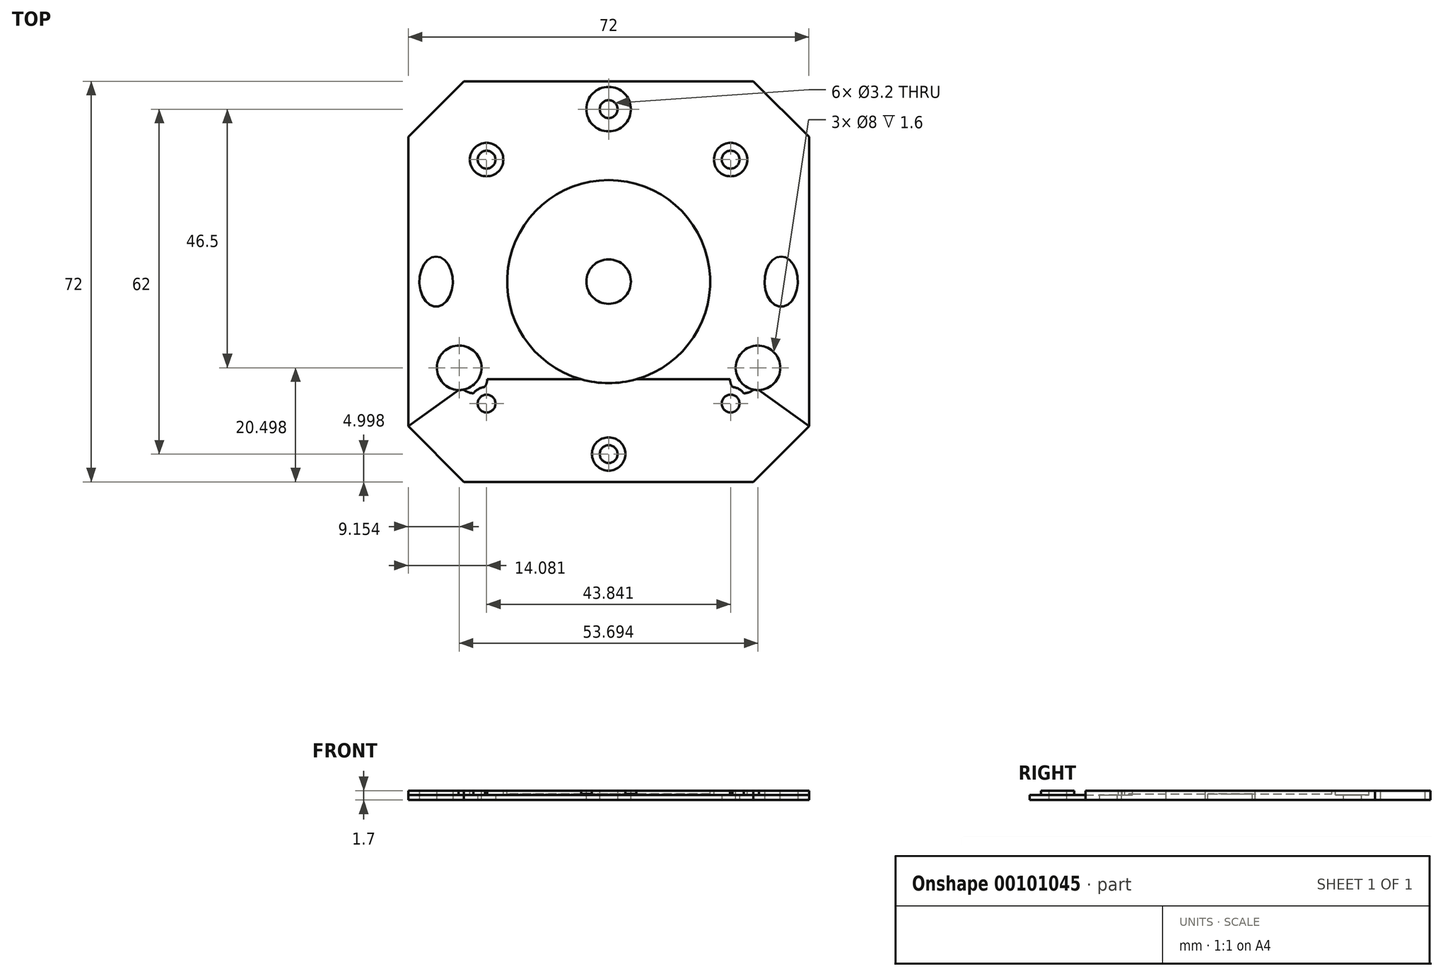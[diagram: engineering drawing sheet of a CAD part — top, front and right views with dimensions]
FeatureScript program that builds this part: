
annotation { "Feature Type Name" : "Feature", "Feature Type Description" : "" }
export const myFeature = defineFeature(function(context is Context, id is Id, definition is map)
    precondition{}
    {
        {
            var Q0;
            Q0=qCreatedBy(makeId("Top.planeOp"),FACE);
            var sketch = newSketch(context, id + "F0", { "sketchPlane" : qUnion([Q0])});
            skLineSegment(sketch, "E0.bottom", {"start": v(-39.14, 42.5) * mm, "end": v(12.86, 42.5) * mm});
            skLineSegment(sketch, "E0.top", {"start": v(-39.14, -29.5) * mm, "end": v(12.86, -29.5) * mm});
            skLineSegment(sketch, "E0.left", {"start": v(-49.14, 32.5) * mm, "end": v(-49.14, -19.5) * mm});
            skLineSegment(sketch, "E0.right", {"start": v(22.86, 32.5) * mm, "end": v(22.86, -19.5) * mm});
            skLineSegment(sketch, "E1", {"start": v(-49.14, 42.5) * mm, "end": v(22.86, -29.5) * mm, "construction": true});
            skLineSegment(sketch, "E2", {"start": v(22.86, 42.5) * mm, "end": v(-49.14, -29.5) * mm, "construction": true});
            skLineSegment(sketch, "E3.bottom", {"start": v(-35.06, 28.43) * mm, "end": v(8.78, 28.43) * mm});
            skLineSegment(sketch, "E3.top", {"start": v(-35.06, -15.41) * mm, "end": v(8.78, -15.41) * mm});
            skLineSegment(sketch, "E3.left", {"start": v(-35.06, 28.43) * mm, "end": v(-35.06, -15.41) * mm});
            skLineSegment(sketch, "E3.right", {"start": v(8.78, 28.43) * mm, "end": v(8.78, -15.41) * mm});
            skCircle(sketch, "E4", {"center": v(-35.06, 28.43) * mm, "radius": 1.6 * mm});
            skCircle(sketch, "E5", {"center": v(8.78, 28.43) * mm, "radius": 1.6 * mm});
            skCircle(sketch, "E6", {"center": v(8.78, -15.41) * mm, "radius": 1.6 * mm});
            skCircle(sketch, "E7", {"center": v(-35.06, -15.41) * mm, "radius": 1.6 * mm});
            skLineSegment(sketch, "E8", {"start": v(-13.14, 42.5) * mm, "end": v(-13.14, -29.5) * mm, "construction": true});
            skLineSegment(sketch, "E9", {"start": v(-49.14, 6.5) * mm, "end": v(22.86, 6.5) * mm, "construction": true});
            skLineSegment(sketch, "E10", {"start": v(-44.14, 6.5) * mm, "end": v(-13.14, 37.5) * mm});
            skLineSegment(sketch, "E11", {"start": v(-13.14, 37.5) * mm, "end": v(17.86, 6.5) * mm});
            skLineSegment(sketch, "E12", {"start": v(-13.14, -24.5) * mm, "end": v(17.86, 6.5) * mm});
            skLineSegment(sketch, "E13", {"start": v(-13.14, -24.5) * mm, "end": v(-44.14, 6.5) * mm});
            skCircle(sketch, "E14", {"center": v(-13.14, 37.5) * mm, "radius": 1.6 * mm});
            skCircle(sketch, "E15", {"center": v(17.86, 6.5) * mm, "radius": 1.6 * mm});
            skCircle(sketch, "E16", {"center": v(-13.14, -24.5) * mm, "radius": 1.6 * mm});
            skCircle(sketch, "E17", {"center": v(-44.14, 6.5) * mm, "radius": 1.6 * mm});
            skCircle(sketch, "E18", {"center": v(-13.14, 6.5) * mm, "radius": 18.25 * mm});
            skPoint(sketch, "E19.visualSharp", {"position": v(-49.14, 42.5) * mm});
            skPoint(sketch, "E20.visualSharp", {"position": v(22.86, 42.5) * mm});
            skPoint(sketch, "E21.visualSharp", {"position": v(22.86, -29.5) * mm});
            skPoint(sketch, "E22.visualSharp", {"position": v(-49.14, -29.5) * mm});
            skLineSegment(sketch, "E23", {"start": v(-39.14, 42.5) * mm, "end": v(-49.14, 32.5) * mm});
            skLineSegment(sketch, "E24", {"start": v(12.86, 42.5) * mm, "end": v(22.86, 32.5) * mm});
            skLineSegment(sketch, "E25", {"start": v(22.86, -19.5) * mm, "end": v(12.86, -29.5) * mm});
            skLineSegment(sketch, "E26", {"start": v(-39.14, -29.5) * mm, "end": v(-49.14, -19.5) * mm});
            skSolve(sketch);
        }
        {
            var Q0;
            Q0=makeQuery(id+"F0.imprint","IMPRINT",FACE,{"disambiguationData":[TD([[makeQuery(id+"F0.imprint","IMPRINT",EDGE,{"derivedFrom":sQuery(id+"F0.wireOp",EDGE,"E0.bottom")}),-1.0]])]});
            var Q1;
            {var subQ0=sQuery(id+"F0.wireOp",EDGE,"E4");var subQ1=sQuery(id+"F0.wireOp",EDGE,"E3.bottom");var subQ2=makeQuery(id+"F0.imprint","INTERSECT",VERTEX,{"derivedFrom":[subQ1,subQ0]});Q1=makeQuery(id+"F0.imprint","IMPRINT",FACE,{"disambiguationData":[TD([[makeQuery(id+"F0.imprint","IMPRINT",EDGE,{"disambiguationData":[TD([[subQ2,-1.0]])],"derivedFrom":subQ1}),-1.0]])]});}
            var Q2;
            {var subQ0=sQuery(id+"F0.wireOp",EDGE,"E10");var subQ1=sQuery(id+"F0.wireOp",EDGE,"E3.bottom");var subQ2=makeQuery(id+"F0.imprint","INTERSECT",VERTEX,{"derivedFrom":[subQ1,subQ0]});Q2=makeQuery(id+"F0.imprint","IMPRINT",FACE,{"disambiguationData":[TD([[makeQuery(id+"F0.imprint","IMPRINT",EDGE,{"disambiguationData":[TD([[subQ2,-1.0]])],"derivedFrom":subQ1}),1.0]])]});}
            var Q3;
            {var subQ0=sQuery(id+"F0.wireOp",EDGE,"E11");var subQ1=sQuery(id+"F0.wireOp",EDGE,"E3.bottom");var subQ2=makeQuery(id+"F0.imprint","INTERSECT",VERTEX,{"derivedFrom":[subQ1,subQ0]});Q3=makeQuery(id+"F0.imprint","IMPRINT",FACE,{"disambiguationData":[TD([[makeQuery(id+"F0.imprint","IMPRINT",EDGE,{"disambiguationData":[TD([[subQ2,-1.0]])],"derivedFrom":subQ1}),-1.0]])]});}
            var Q4;
            {var subQ0=sQuery(id+"F0.wireOp",EDGE,"E11");var subQ1=sQuery(id+"F0.wireOp",EDGE,"E3.right");var subQ2=makeQuery(id+"F0.imprint","INTERSECT",VERTEX,{"derivedFrom":[subQ1,subQ0]});Q4=makeQuery(id+"F0.imprint","IMPRINT",FACE,{"disambiguationData":[TD([[makeQuery(id+"F0.imprint","IMPRINT",EDGE,{"disambiguationData":[TD([[subQ2,-1.0]])],"derivedFrom":subQ1}),1.0]])]});}
            var Q5;
            {var subQ0=sQuery(id+"F0.wireOp",EDGE,"E12");var subQ1=sQuery(id+"F0.wireOp",EDGE,"E3.top");var subQ2=makeQuery(id+"F0.imprint","INTERSECT",VERTEX,{"derivedFrom":[subQ1,subQ0]});Q5=makeQuery(id+"F0.imprint","IMPRINT",FACE,{"disambiguationData":[TD([[makeQuery(id+"F0.imprint","IMPRINT",EDGE,{"disambiguationData":[TD([[subQ2,-1.0]])],"derivedFrom":subQ1}),1.0]])]});}
            var Q6;
            {var subQ0=sQuery(id+"F0.wireOp",EDGE,"E13");var subQ1=sQuery(id+"F0.wireOp",EDGE,"E3.top");var subQ2=makeQuery(id+"F0.imprint","INTERSECT",VERTEX,{"derivedFrom":[subQ1,subQ0]});Q6=makeQuery(id+"F0.imprint","IMPRINT",FACE,{"disambiguationData":[TD([[makeQuery(id+"F0.imprint","IMPRINT",EDGE,{"disambiguationData":[TD([[subQ2,-1.0]])],"derivedFrom":subQ1}),-1.0]])]});}
            var Q7;
            {var subQ0=sQuery(id+"F0.wireOp",EDGE,"E7");var subQ1=sQuery(id+"F0.wireOp",EDGE,"E3.top");var subQ2=makeQuery(id+"F0.imprint","INTERSECT",VERTEX,{"derivedFrom":[subQ1,subQ0]});Q7=makeQuery(id+"F0.imprint","IMPRINT",FACE,{"disambiguationData":[TD([[makeQuery(id+"F0.imprint","IMPRINT",EDGE,{"disambiguationData":[TD([[subQ2,-1.0]])],"derivedFrom":subQ1}),1.0]])]});}
            var Q8;
            {var subQ0=sQuery(id+"F0.wireOp",EDGE,"E10");var subQ1=sQuery(id+"F0.wireOp",EDGE,"E3.left");var subQ2=makeQuery(id+"F0.imprint","INTERSECT",VERTEX,{"derivedFrom":[subQ1,subQ0]});Q8=makeQuery(id+"F0.imprint","IMPRINT",FACE,{"disambiguationData":[TD([[makeQuery(id+"F0.imprint","IMPRINT",EDGE,{"disambiguationData":[TD([[subQ2,-1.0]])],"derivedFrom":subQ1}),-1.0]])]});}
            var Q9;
            Q9=makeQuery(id+"F0.imprint","IMPRINT",FACE,{"disambiguationData":[TD([[makeQuery(id+"F0.imprint","IMPRINT",EDGE,{"derivedFrom":sQuery(id+"F0.wireOp",EDGE,"E18")}),-1.0]])]});
            var Q10;
            Q10=makeQuery(id+"F0.imprint","IMPRINT",FACE,{"disambiguationData":[TD([[makeQuery(id+"F0.imprint","IMPRINT",EDGE,{"derivedFrom":sQuery(id+"F0.wireOp",EDGE,"E18")}),1.0]])]});
            extrude(context, id + "F1", {"entities" : qUnion([Q0, Q1, Q2, Q3, Q4, Q5, Q6, Q7, Q8, Q9, Q10]), "depth" : 1.7 * mm});
        }
        {
            var Q0;
            Q0=makeQuery(id+"F1.opExtrude","CAP_FACE",FACE,{"disambiguationData":[OSD([sQuery(id+"F0.wireOp",EDGE,"E0.bottom"),sQuery(id+"F0.wireOp",EDGE,"E0.top"),sQuery(id+"F0.wireOp",EDGE,"E0.left"),sQuery(id+"F0.wireOp",EDGE,"E0.right"),sQuery(id+"F0.wireOp",EDGE,"E4"),sQuery(id+"F0.wireOp",EDGE,"E5"),sQuery(id+"F0.wireOp",EDGE,"E6"),sQuery(id+"F0.wireOp",EDGE,"E7"),sQuery(id+"F0.wireOp",EDGE,"E14"),sQuery(id+"F0.wireOp",EDGE,"E15"),sQuery(id+"F0.wireOp",EDGE,"E16"),sQuery(id+"F0.wireOp",EDGE,"E17"),sQuery(id+"F0.wireOp",EDGE,"E23"),sQuery(id+"F0.wireOp",EDGE,"E24"),sQuery(id+"F0.wireOp",EDGE,"E25"),sQuery(id+"F0.wireOp",EDGE,"E26")])],"isStart":false});
            var sketch = newSketch(context, id + "F2", { "sketchPlane" : qUnion([Q0])});
            skLineSegment(sketch, "E27", {"start": v(-49.14, 6.5) * mm, "end": v(22.86, 6.5) * mm});
            skLineSegment(sketch, "E28", {"start": v(-13.14, -29.5) * mm, "end": v(-13.14, 42.5) * mm});
            skCircle(sketch, "E29", {"center": v(-13.14, 6.5) * mm, "radius": 18.25 * mm});
            skSolve(sketch);
        }
        {
            var Q0;
            {var subQ0=sQuery(id+"F2.wireOp",EDGE,"E29");var subQ1=sQuery(id+"F2.wireOp",EDGE,"E27");var subQ2=makeQuery(id+"F2.imprint","INTERSECT",VERTEX,{"disambiguationData":[OD(0.0)],"derivedFrom":[subQ1,subQ0]});Q0=makeQuery(id+"F2.imprint","IMPRINT",FACE,{"disambiguationData":[TD([[makeQuery(id+"F2.imprint","IMPRINT",EDGE,{"disambiguationData":[TD([[subQ2,-1.0]])],"derivedFrom":subQ1}),1.0]])]});}
            var Q1;
            {var subQ0=sQuery(id+"F2.wireOp",EDGE,"E28");var subQ1=sQuery(id+"F2.wireOp",EDGE,"E27");var subQ2=makeQuery(id+"F2.imprint","INTERSECT",VERTEX,{"derivedFrom":[subQ1,subQ0]});Q1=makeQuery(id+"F2.imprint","IMPRINT",FACE,{"disambiguationData":[TD([[makeQuery(id+"F2.imprint","IMPRINT",EDGE,{"disambiguationData":[TD([[subQ2,-1.0]])],"derivedFrom":subQ1}),-1.0]])]});}
            var Q2;
            {var subQ0=sQuery(id+"F2.wireOp",EDGE,"E28");var subQ1=sQuery(id+"F2.wireOp",EDGE,"E27");var subQ2=makeQuery(id+"F2.imprint","INTERSECT",VERTEX,{"derivedFrom":[subQ1,subQ0]});Q2=makeQuery(id+"F2.imprint","IMPRINT",FACE,{"disambiguationData":[TD([[makeQuery(id+"F2.imprint","IMPRINT",EDGE,{"disambiguationData":[TD([[subQ2,-1.0]])],"derivedFrom":subQ1}),1.0]])]});}
            var Q3;
            {var subQ0=sQuery(id+"F2.wireOp",EDGE,"E29");var subQ1=sQuery(id+"F2.wireOp",EDGE,"E27");var subQ2=makeQuery(id+"F2.imprint","INTERSECT",VERTEX,{"disambiguationData":[OD(0.0)],"derivedFrom":[subQ1,subQ0]});Q3=makeQuery(id+"F2.imprint","IMPRINT",FACE,{"disambiguationData":[TD([[makeQuery(id+"F2.imprint","IMPRINT",EDGE,{"disambiguationData":[TD([[subQ2,-1.0]])],"derivedFrom":subQ1}),-1.0]])]});}
            extrude(context, id + "F3", {"entities" : qUnion([Q0, Q1, Q2, Q3]), "operationType" : NewBodyOperationType.REMOVE, "oppositeDirection" : true, "depth" : 0.6 * mm});
        }
        {
            var Q0;
            Q0=makeQuery(id+"F1.opExtrude","CAP_FACE",FACE,{"disambiguationData":[OSD([sQuery(id+"F0.wireOp",EDGE,"E0.bottom"),sQuery(id+"F0.wireOp",EDGE,"E0.top"),sQuery(id+"F0.wireOp",EDGE,"E0.left"),sQuery(id+"F0.wireOp",EDGE,"E0.right"),sQuery(id+"F0.wireOp",EDGE,"E4"),sQuery(id+"F0.wireOp",EDGE,"E5"),sQuery(id+"F0.wireOp",EDGE,"E6"),sQuery(id+"F0.wireOp",EDGE,"E7"),sQuery(id+"F0.wireOp",EDGE,"E14"),sQuery(id+"F0.wireOp",EDGE,"E15"),sQuery(id+"F0.wireOp",EDGE,"E16"),sQuery(id+"F0.wireOp",EDGE,"E17"),sQuery(id+"F0.wireOp",EDGE,"E23"),sQuery(id+"F0.wireOp",EDGE,"E24"),sQuery(id+"F0.wireOp",EDGE,"E25"),sQuery(id+"F0.wireOp",EDGE,"E26")])],"isStart":false});
            var sketch = newSketch(context, id + "F4", { "sketchPlane" : qUnion([Q0])});
            skLineSegment(sketch, "E30", {"start": v(-49.14, 6.5) * mm, "end": v(22.86, 6.5) * mm});
            skLineSegment(sketch, "E31", {"start": v(-13.14, -29.5) * mm, "end": v(-13.14, 42.5) * mm});
            skCircle(sketch, "E32", {"center": v(-13.14, 6.5) * mm, "radius": 3.5 * mm});
            skLineSegment(sketch, "E33", {"start": v(-49.14, -19.5) * mm, "end": v(22.86, 32.5) * mm});
            skLineSegment(sketch, "E34", {"start": v(22.86, -19.5) * mm, "end": v(-49.14, 32.5) * mm});
            skLineSegment(sketch, "E35", {"start": v(-13.14, 6.5) * mm, "end": v(-37.46, -11.06) * mm});
            skLineSegment(sketch, "E36", {"start": v(-13.14, 6.5) * mm, "end": v(11.18, 24.07) * mm});
            skLineSegment(sketch, "E37.bottom", {"start": v(-37.46, -11.06) * mm, "end": v(11.18, -11.06) * mm});
            skLineSegment(sketch, "E37.top", {"start": v(-37.46, 24.07) * mm, "end": v(11.18, 24.07) * mm});
            skLineSegment(sketch, "E37.left", {"start": v(-37.46, -11.06) * mm, "end": v(-37.46, 24.07) * mm});
            skLineSegment(sketch, "E37.right", {"start": v(11.18, -11.06) * mm, "end": v(11.18, 24.07) * mm});
            skCircle(sketch, "E38", {"center": v(-37.46, -11.06) * mm, "radius": 2.5 * mm});
            skCircle(sketch, "E39", {"center": v(11.18, -11.06) * mm, "radius": 2.5 * mm});
            skCircle(sketch, "E40", {"center": v(-13.14, 37.5) * mm, "radius": 3 * mm});
            skCircle(sketch, "E41", {"center": v(17.86, 6.5) * mm, "radius": 3 * mm});
            skCircle(sketch, "E42", {"center": v(-44.14, 6.5) * mm, "radius": 3 * mm});
            skCircle(sketch, "E43", {"center": v(-13.14, -24.5) * mm, "radius": 3 * mm});
            skCircle(sketch, "E44", {"center": v(8.78, -15.41) * mm, "radius": 3 * mm});
            skCircle(sketch, "E45", {"center": v(-35.06, 28.43) * mm, "radius": 3 * mm});
            skCircle(sketch, "E46", {"center": v(-35.06, -15.41) * mm, "radius": 3 * mm});
            skCircle(sketch, "E47", {"center": v(8.78, 28.43) * mm, "radius": 3 * mm});
            skSolve(sketch);
        }
        {
            var Q0;
            Q0=makeQuery(id+"F4.imprint","IMPRINT",FACE,{"disambiguationData":[TD([[makeQuery(id+"F4.imprint","IMPRINT",EDGE,{"derivedFrom":makeQuery(id+"F1.opExtrude","CAP_EDGE",EDGE,{"disambiguationData":[OSD([sQuery(id+"F0.wireOp",EDGE,"E4")])],"isStart":false})}),1.0]])]});
            var Q1;
            Q1=makeQuery(id+"F4.imprint","IMPRINT",FACE,{"disambiguationData":[TD([[makeQuery(id+"F4.imprint","IMPRINT",EDGE,{"derivedFrom":makeQuery(id+"F1.opExtrude","CAP_EDGE",EDGE,{"disambiguationData":[OSD([sQuery(id+"F0.wireOp",EDGE,"E5")])],"isStart":false})}),1.0]])]});
            var Q2;
            Q2=makeQuery(id+"F4.imprint","IMPRINT",FACE,{"disambiguationData":[TD([[makeQuery(id+"F4.imprint","IMPRINT",EDGE,{"derivedFrom":makeQuery(id+"F1.opExtrude","CAP_EDGE",EDGE,{"disambiguationData":[OSD([sQuery(id+"F0.wireOp",EDGE,"E6")])],"isStart":false})}),1.0]])]});
            var Q3;
            Q3=makeQuery(id+"F4.imprint","IMPRINT",FACE,{"disambiguationData":[TD([[makeQuery(id+"F4.imprint","IMPRINT",EDGE,{"derivedFrom":makeQuery(id+"F1.opExtrude","CAP_EDGE",EDGE,{"disambiguationData":[OSD([sQuery(id+"F0.wireOp",EDGE,"E7")])],"isStart":false})}),1.0]])]});
            var Q4;
            {var subQ0=sQuery(id+"F4.wireOp",EDGE,"E46");var subQ1=sQuery(id+"F4.wireOp",EDGE,"E38");var subQ2=makeQuery(id+"F4.imprint","INTERSECT",VERTEX,{"disambiguationData":[OD(0.0)],"derivedFrom":[subQ1,subQ0]});Q4=makeQuery(id+"F4.imprint","IMPRINT",FACE,{"disambiguationData":[TD([[makeQuery(id+"F4.imprint","IMPRINT",EDGE,{"disambiguationData":[TD([[subQ2,-1.0]])],"derivedFrom":subQ1}),1.0]])]});}
            var Q5;
            {var subQ0=sQuery(id+"F4.wireOp",EDGE,"E44");var subQ1=sQuery(id+"F4.wireOp",EDGE,"E39");var subQ2=makeQuery(id+"F4.imprint","INTERSECT",VERTEX,{"disambiguationData":[OD(0.0)],"derivedFrom":[subQ1,subQ0]});Q5=makeQuery(id+"F4.imprint","IMPRINT",FACE,{"disambiguationData":[TD([[makeQuery(id+"F4.imprint","IMPRINT",EDGE,{"disambiguationData":[TD([[subQ2,-1.0]])],"derivedFrom":subQ1}),1.0]])]});}
            var Q6;
            Q6=makeQuery(id+"F4.imprint","IMPRINT",FACE,{"disambiguationData":[TD([[makeQuery(id+"F4.imprint","IMPRINT",EDGE,{"derivedFrom":sQuery(id+"F4.wireOp",EDGE,"E45")}),1.0]])]});
            var Q7;
            Q7=makeQuery(id+"F4.imprint","IMPRINT",FACE,{"disambiguationData":[TD([[makeQuery(id+"F4.imprint","IMPRINT",EDGE,{"derivedFrom":sQuery(id+"F4.wireOp",EDGE,"E47")}),1.0]])]});
            var Q8;
            {var subQ1=sQuery(id+"F4.wireOp",EDGE,"E33");var subQ3=sQuery(id+"F4.wireOp",EDGE,"E38");var subQ4=makeQuery(id+"F4.imprint","INTERSECT",VERTEX,{"derivedFrom":[subQ1,subQ3]});Q8=makeQuery(id+"F4.imprint","IMPRINT",FACE,{"disambiguationData":[TD([[makeQuery(id+"F4.imprint","IMPRINT",EDGE,{"disambiguationData":[TD([[subQ4,1.0]])],"derivedFrom":subQ3}),1.0]])]});}
            var Q9;
            {var subQ1=sQuery(id+"F4.wireOp",EDGE,"E34");var subQ3=sQuery(id+"F4.wireOp",EDGE,"E39");var subQ4=makeQuery(id+"F4.imprint","INTERSECT",VERTEX,{"disambiguationData":[OD(0.0)],"derivedFrom":[subQ1,subQ3]});Q9=makeQuery(id+"F4.imprint","IMPRINT",FACE,{"disambiguationData":[TD([[makeQuery(id+"F4.imprint","IMPRINT",EDGE,{"disambiguationData":[TD([[subQ4,-1.0]])],"derivedFrom":subQ3}),1.0]])]});}
            var Q10;
            {var subQ1=sQuery(id+"F4.wireOp",EDGE,"E34");var subQ3=sQuery(id+"F4.wireOp",EDGE,"E39");var subQ4=makeQuery(id+"F4.imprint","INTERSECT",VERTEX,{"disambiguationData":[OD(1.0)],"derivedFrom":[subQ1,subQ3]});Q10=makeQuery(id+"F4.imprint","IMPRINT",FACE,{"disambiguationData":[TD([[makeQuery(id+"F4.imprint","IMPRINT",EDGE,{"disambiguationData":[TD([[subQ4,-1.0]])],"derivedFrom":subQ3}),1.0]])]});}
            var Q11;
            {var subQ1=sQuery(id+"F4.wireOp",EDGE,"E34");var subQ3=sQuery(id+"F4.wireOp",EDGE,"E39");var subQ4=makeQuery(id+"F4.imprint","INTERSECT",VERTEX,{"disambiguationData":[OD(1.0)],"derivedFrom":[subQ1,subQ3]});Q11=makeQuery(id+"F4.imprint","IMPRINT",FACE,{"disambiguationData":[TD([[makeQuery(id+"F4.imprint","IMPRINT",EDGE,{"disambiguationData":[TD([[subQ4,1.0]])],"derivedFrom":subQ3}),1.0]])]});}
            var Q12;
            {var subQ1=sQuery(id+"F4.wireOp",EDGE,"E35");var subQ3=sQuery(id+"F4.wireOp",EDGE,"E38");var subQ4=makeQuery(id+"F4.imprint","INTERSECT",VERTEX,{"derivedFrom":[subQ1,subQ3]});Q12=makeQuery(id+"F4.imprint","IMPRINT",FACE,{"disambiguationData":[TD([[makeQuery(id+"F4.imprint","IMPRINT",EDGE,{"disambiguationData":[TD([[subQ4,1.0]])],"derivedFrom":subQ3}),1.0]])]});}
            var Q13;
            {var subQ1=sQuery(id+"F4.wireOp",EDGE,"E35");var subQ3=sQuery(id+"F4.wireOp",EDGE,"E38");var subQ4=makeQuery(id+"F4.imprint","INTERSECT",VERTEX,{"derivedFrom":[subQ1,subQ3]});Q13=makeQuery(id+"F4.imprint","IMPRINT",FACE,{"disambiguationData":[TD([[makeQuery(id+"F4.imprint","IMPRINT",EDGE,{"disambiguationData":[TD([[subQ4,-1.0]])],"derivedFrom":subQ3}),1.0]])]});}
            var Q14;
            Q14=makeQuery(id+"F4.imprint","IMPRINT",FACE,{"disambiguationData":[TD([[makeQuery(id+"F4.imprint","IMPRINT",EDGE,{"derivedFrom":makeQuery(id+"F1.opExtrude","CAP_EDGE",EDGE,{"disambiguationData":[OSD([sQuery(id+"F0.wireOp",EDGE,"E7")])],"isStart":false})}),-1.0]])]});
            var Q15;
            Q15=makeQuery(id+"F4.imprint","IMPRINT",FACE,{"disambiguationData":[TD([[makeQuery(id+"F4.imprint","IMPRINT",EDGE,{"derivedFrom":makeQuery(id+"F1.opExtrude","CAP_EDGE",EDGE,{"disambiguationData":[OSD([sQuery(id+"F0.wireOp",EDGE,"E6")])],"isStart":false})}),-1.0]])]});
            var Q16;
            {var subQ0=sQuery(id+"F4.wireOp",EDGE,"E38");var subQ6=sQuery(id+"F4.wireOp",EDGE,"E33");var subQ7=makeQuery(id+"F4.imprint","INTERSECT",VERTEX,{"derivedFrom":[subQ6,subQ0]});Q16=makeQuery(id+"F4.imprint","IMPRINT",FACE,{"disambiguationData":[TD([[makeQuery(id+"F4.imprint","IMPRINT",EDGE,{"disambiguationData":[TD([[subQ7,-1.0]])],"derivedFrom":subQ0}),1.0]])]});}
            var Q17;
            {var subQ0=sQuery(id+"F4.wireOp",EDGE,"E39");var subQ5=sQuery(id+"F4.wireOp",EDGE,"E37.bottom");var subQ6=makeQuery(id+"F4.imprint","INTERSECT",VERTEX,{"derivedFrom":[subQ5,subQ0]});Q17=makeQuery(id+"F4.imprint","IMPRINT",FACE,{"disambiguationData":[TD([[makeQuery(id+"F4.imprint","IMPRINT",EDGE,{"disambiguationData":[TD([[subQ6,-1.0]])],"derivedFrom":subQ0}),1.0]])]});}
            var Q18;
            {var subQ0=sQuery(id+"F4.wireOp",EDGE,"E42");var subQ1=sQuery(id+"F4.wireOp",EDGE,"E30");var subQ2=makeQuery(id+"F4.imprint","INTERSECT",VERTEX,{"disambiguationData":[OD(0.0)],"derivedFrom":[subQ1,subQ0]});Q18=makeQuery(id+"F4.imprint","IMPRINT",FACE,{"disambiguationData":[TD([[makeQuery(id+"F4.imprint","IMPRINT",EDGE,{"disambiguationData":[TD([[subQ2,-1.0]])],"derivedFrom":subQ1}),1.0]])]});}
            var Q19;
            {var subQ0=sQuery(id+"F4.wireOp",EDGE,"E42");var subQ1=sQuery(id+"F4.wireOp",EDGE,"E30");var subQ2=makeQuery(id+"F4.imprint","INTERSECT",VERTEX,{"disambiguationData":[OD(0.0)],"derivedFrom":[subQ1,subQ0]});Q19=makeQuery(id+"F4.imprint","IMPRINT",FACE,{"disambiguationData":[TD([[makeQuery(id+"F4.imprint","IMPRINT",EDGE,{"disambiguationData":[TD([[subQ2,-1.0]])],"derivedFrom":subQ1}),-1.0]])]});}
            var Q20;
            {var subQ0=sQuery(id+"F4.wireOp",EDGE,"E41");var subQ1=sQuery(id+"F4.wireOp",EDGE,"E30");var subQ2=makeQuery(id+"F4.imprint","INTERSECT",VERTEX,{"disambiguationData":[OD(0.0)],"derivedFrom":[subQ1,subQ0]});Q20=makeQuery(id+"F4.imprint","IMPRINT",FACE,{"disambiguationData":[TD([[makeQuery(id+"F4.imprint","IMPRINT",EDGE,{"disambiguationData":[TD([[subQ2,-1.0]])],"derivedFrom":subQ1}),1.0]])]});}
            var Q21;
            {var subQ0=sQuery(id+"F4.wireOp",EDGE,"E41");var subQ1=sQuery(id+"F4.wireOp",EDGE,"E30");var subQ2=makeQuery(id+"F4.imprint","INTERSECT",VERTEX,{"disambiguationData":[OD(0.0)],"derivedFrom":[subQ1,subQ0]});Q21=makeQuery(id+"F4.imprint","IMPRINT",FACE,{"disambiguationData":[TD([[makeQuery(id+"F4.imprint","IMPRINT",EDGE,{"disambiguationData":[TD([[subQ2,-1.0]])],"derivedFrom":subQ1}),-1.0]])]});}
            var Q22;
            {var subQ0=sQuery(id+"F4.wireOp",EDGE,"E43");var subQ1=sQuery(id+"F4.wireOp",EDGE,"E31");var subQ2=makeQuery(id+"F4.imprint","INTERSECT",VERTEX,{"disambiguationData":[OD(0.0)],"derivedFrom":[subQ1,subQ0]});Q22=makeQuery(id+"F4.imprint","IMPRINT",FACE,{"disambiguationData":[TD([[makeQuery(id+"F4.imprint","IMPRINT",EDGE,{"disambiguationData":[TD([[subQ2,-1.0]])],"derivedFrom":subQ1}),1.0]])]});}
            var Q23;
            {var subQ0=sQuery(id+"F4.wireOp",EDGE,"E43");var subQ1=sQuery(id+"F4.wireOp",EDGE,"E31");var subQ2=makeQuery(id+"F4.imprint","INTERSECT",VERTEX,{"disambiguationData":[OD(0.0)],"derivedFrom":[subQ1,subQ0]});Q23=makeQuery(id+"F4.imprint","IMPRINT",FACE,{"disambiguationData":[TD([[makeQuery(id+"F4.imprint","IMPRINT",EDGE,{"disambiguationData":[TD([[subQ2,-1.0]])],"derivedFrom":subQ1}),-1.0]])]});}
            var Q24;
            {var subQ0=sQuery(id+"F4.wireOp",EDGE,"E40");var subQ1=sQuery(id+"F4.wireOp",EDGE,"E31");var subQ2=makeQuery(id+"F4.imprint","INTERSECT",VERTEX,{"disambiguationData":[OD(0.0)],"derivedFrom":[subQ1,subQ0]});Q24=makeQuery(id+"F4.imprint","IMPRINT",FACE,{"disambiguationData":[TD([[makeQuery(id+"F4.imprint","IMPRINT",EDGE,{"disambiguationData":[TD([[subQ2,-1.0]])],"derivedFrom":subQ1}),1.0]])]});}
            var Q25;
            {var subQ0=sQuery(id+"F4.wireOp",EDGE,"E40");var subQ1=sQuery(id+"F4.wireOp",EDGE,"E31");var subQ2=makeQuery(id+"F4.imprint","INTERSECT",VERTEX,{"disambiguationData":[OD(0.0)],"derivedFrom":[subQ1,subQ0]});Q25=makeQuery(id+"F4.imprint","IMPRINT",FACE,{"disambiguationData":[TD([[makeQuery(id+"F4.imprint","IMPRINT",EDGE,{"disambiguationData":[TD([[subQ2,-1.0]])],"derivedFrom":subQ1}),-1.0]])]});}
            var Q26;
            {var subQ0=sQuery(id+"F4.wireOp",EDGE,"E30");var subQ1=makeQuery(id+"F1.opExtrude","CAP_EDGE",EDGE,{"disambiguationData":[OSD([sQuery(id+"F0.wireOp",EDGE,"E17")])],"isStart":false});var subQ2=makeQuery(id+"F4.imprint","INTERSECT",VERTEX,{"disambiguationData":[OD(0.0)],"derivedFrom":[subQ1,subQ0]});Q26=makeQuery(id+"F4.imprint","IMPRINT",FACE,{"disambiguationData":[TD([[makeQuery(id+"F4.imprint","IMPRINT",EDGE,{"disambiguationData":[TD([[subQ2,-1.0]])],"derivedFrom":subQ0}),1.0]])]});}
            var Q27;
            {var subQ0=sQuery(id+"F4.wireOp",EDGE,"E30");var subQ1=makeQuery(id+"F1.opExtrude","CAP_EDGE",EDGE,{"disambiguationData":[OSD([sQuery(id+"F0.wireOp",EDGE,"E17")])],"isStart":false});var subQ2=makeQuery(id+"F4.imprint","INTERSECT",VERTEX,{"disambiguationData":[OD(0.0)],"derivedFrom":[subQ1,subQ0]});Q27=makeQuery(id+"F4.imprint","IMPRINT",FACE,{"disambiguationData":[TD([[makeQuery(id+"F4.imprint","IMPRINT",EDGE,{"disambiguationData":[TD([[subQ2,-1.0]])],"derivedFrom":subQ0}),-1.0]])]});}
            var Q28;
            {var subQ0=sQuery(id+"F4.wireOp",EDGE,"E30");var subQ1=makeQuery(id+"F1.opExtrude","CAP_EDGE",EDGE,{"disambiguationData":[OSD([sQuery(id+"F0.wireOp",EDGE,"E15")])],"isStart":false});var subQ2=makeQuery(id+"F4.imprint","INTERSECT",VERTEX,{"disambiguationData":[OD(0.0)],"derivedFrom":[subQ1,subQ0]});Q28=makeQuery(id+"F4.imprint","IMPRINT",FACE,{"disambiguationData":[TD([[makeQuery(id+"F4.imprint","IMPRINT",EDGE,{"disambiguationData":[TD([[subQ2,-1.0]])],"derivedFrom":subQ0}),1.0]])]});}
            var Q29;
            {var subQ0=sQuery(id+"F4.wireOp",EDGE,"E30");var subQ1=makeQuery(id+"F1.opExtrude","CAP_EDGE",EDGE,{"disambiguationData":[OSD([sQuery(id+"F0.wireOp",EDGE,"E15")])],"isStart":false});var subQ2=makeQuery(id+"F4.imprint","INTERSECT",VERTEX,{"disambiguationData":[OD(0.0)],"derivedFrom":[subQ1,subQ0]});Q29=makeQuery(id+"F4.imprint","IMPRINT",FACE,{"disambiguationData":[TD([[makeQuery(id+"F4.imprint","IMPRINT",EDGE,{"disambiguationData":[TD([[subQ2,-1.0]])],"derivedFrom":subQ0}),-1.0]])]});}
            var Q30;
            {var subQ0=sQuery(id+"F4.wireOp",EDGE,"E31");var subQ1=makeQuery(id+"F1.opExtrude","CAP_EDGE",EDGE,{"disambiguationData":[OSD([sQuery(id+"F0.wireOp",EDGE,"E16")])],"isStart":false});var subQ2=makeQuery(id+"F4.imprint","INTERSECT",VERTEX,{"disambiguationData":[OD(0.0)],"derivedFrom":[subQ1,subQ0]});Q30=makeQuery(id+"F4.imprint","IMPRINT",FACE,{"disambiguationData":[TD([[makeQuery(id+"F4.imprint","IMPRINT",EDGE,{"disambiguationData":[TD([[subQ2,-1.0]])],"derivedFrom":subQ0}),1.0]])]});}
            var Q31;
            {var subQ0=sQuery(id+"F4.wireOp",EDGE,"E31");var subQ1=makeQuery(id+"F1.opExtrude","CAP_EDGE",EDGE,{"disambiguationData":[OSD([sQuery(id+"F0.wireOp",EDGE,"E16")])],"isStart":false});var subQ2=makeQuery(id+"F4.imprint","INTERSECT",VERTEX,{"disambiguationData":[OD(0.0)],"derivedFrom":[subQ1,subQ0]});Q31=makeQuery(id+"F4.imprint","IMPRINT",FACE,{"disambiguationData":[TD([[makeQuery(id+"F4.imprint","IMPRINT",EDGE,{"disambiguationData":[TD([[subQ2,-1.0]])],"derivedFrom":subQ0}),-1.0]])]});}
            var Q32;
            {var subQ0=sQuery(id+"F4.wireOp",EDGE,"E31");var subQ1=makeQuery(id+"F1.opExtrude","CAP_EDGE",EDGE,{"disambiguationData":[OSD([sQuery(id+"F0.wireOp",EDGE,"E14")])],"isStart":false});var subQ2=makeQuery(id+"F4.imprint","INTERSECT",VERTEX,{"disambiguationData":[OD(0.0)],"derivedFrom":[subQ1,subQ0]});Q32=makeQuery(id+"F4.imprint","IMPRINT",FACE,{"disambiguationData":[TD([[makeQuery(id+"F4.imprint","IMPRINT",EDGE,{"disambiguationData":[TD([[subQ2,-1.0]])],"derivedFrom":subQ0}),1.0]])]});}
            var Q33;
            {var subQ0=sQuery(id+"F4.wireOp",EDGE,"E31");var subQ1=makeQuery(id+"F1.opExtrude","CAP_EDGE",EDGE,{"disambiguationData":[OSD([sQuery(id+"F0.wireOp",EDGE,"E14")])],"isStart":false});var subQ2=makeQuery(id+"F4.imprint","INTERSECT",VERTEX,{"disambiguationData":[OD(0.0)],"derivedFrom":[subQ1,subQ0]});Q33=makeQuery(id+"F4.imprint","IMPRINT",FACE,{"disambiguationData":[TD([[makeQuery(id+"F4.imprint","IMPRINT",EDGE,{"disambiguationData":[TD([[subQ2,-1.0]])],"derivedFrom":subQ0}),-1.0]])]});}
            extrude(context, id + "F5", {"entities" : qUnion([Q0, Q1, Q2, Q3, Q4, Q5, Q6, Q7, Q8, Q9, Q10, Q11, Q12, Q13, Q14, Q15, Q16, Q17, Q18, Q19, Q20, Q21, Q22, Q23, Q24, Q25, Q26, Q27, Q28, Q29, Q30, Q31, Q32, Q33]), "operationType" : NewBodyOperationType.REMOVE, "oppositeDirection" : true, "depth" : 0.8 * mm});
        }
        {
            var Q0;
            Q0=makeQuery(id+"F1.opExtrude","CAP_FACE",FACE,{"disambiguationData":[OSD([sQuery(id+"F0.wireOp",EDGE,"E0.bottom"),sQuery(id+"F0.wireOp",EDGE,"E0.top"),sQuery(id+"F0.wireOp",EDGE,"E0.left"),sQuery(id+"F0.wireOp",EDGE,"E0.right"),sQuery(id+"F0.wireOp",EDGE,"E4"),sQuery(id+"F0.wireOp",EDGE,"E5"),sQuery(id+"F0.wireOp",EDGE,"E6"),sQuery(id+"F0.wireOp",EDGE,"E7"),sQuery(id+"F0.wireOp",EDGE,"E14"),sQuery(id+"F0.wireOp",EDGE,"E15"),sQuery(id+"F0.wireOp",EDGE,"E16"),sQuery(id+"F0.wireOp",EDGE,"E17"),sQuery(id+"F0.wireOp",EDGE,"E23"),sQuery(id+"F0.wireOp",EDGE,"E24"),sQuery(id+"F0.wireOp",EDGE,"E25"),sQuery(id+"F0.wireOp",EDGE,"E26")])],"isStart":false});
            var sketch = newSketch(context, id + "F6", { "sketchPlane" : qUnion([Q0])});
            skLineSegment(sketch, "E48", {"start": v(-13.14, 42.5) * mm, "end": v(-13.14, -29.5) * mm});
            skLineSegment(sketch, "E49", {"start": v(-49.14, 6.5) * mm, "end": v(22.86, 6.5) * mm});
            skCircle(sketch, "E50", {"center": v(-13.14, 6.5) * mm, "radius": 4 * mm});
            skSolve(sketch);
        }
        {
            var Q0;
            Q0 = qSketchRegion(id + "F6", true);
            extrude(context, id + "F7", {"entities" : qUnion([Q0]), "operationType" : NewBodyOperationType.REMOVE, "oppositeDirection" : true, "depth" : 25 * mm});
        }
        {
            var Q0;
            Q0=makeQuery(id+"F1.opExtrude","CAP_FACE",FACE,{"disambiguationData":[OSD([sQuery(id+"F0.wireOp",EDGE,"E0.bottom"),sQuery(id+"F0.wireOp",EDGE,"E0.top"),sQuery(id+"F0.wireOp",EDGE,"E0.left"),sQuery(id+"F0.wireOp",EDGE,"E0.right"),sQuery(id+"F0.wireOp",EDGE,"E4"),sQuery(id+"F0.wireOp",EDGE,"E5"),sQuery(id+"F0.wireOp",EDGE,"E6"),sQuery(id+"F0.wireOp",EDGE,"E7"),sQuery(id+"F0.wireOp",EDGE,"E14"),sQuery(id+"F0.wireOp",EDGE,"E15"),sQuery(id+"F0.wireOp",EDGE,"E16"),sQuery(id+"F0.wireOp",EDGE,"E17"),sQuery(id+"F0.wireOp",EDGE,"E23"),sQuery(id+"F0.wireOp",EDGE,"E24"),sQuery(id+"F0.wireOp",EDGE,"E25"),sQuery(id+"F0.wireOp",EDGE,"E26")])],"isStart":false});
            var sketch = newSketch(context, id + "F8", { "sketchPlane" : qUnion([Q0])});
            skCircle(sketch, "E51", {"center": v(-37.46, -11.06) * mm, "radius": 2.5 * mm});
            skCircle(sketch, "E52", {"center": v(11.18, -11.06) * mm, "radius": 2.5 * mm});
            skSolve(sketch);
        }
        {
            var Q0;
            Q0 = qSketchRegion(id + "F8", true);
            extrude(context, id + "F9", {"entities" : qUnion([Q0]), "operationType" : NewBodyOperationType.ADD, "oppositeDirection" : true, "depth" : 1.6 * mm});
        }
        {
            var Q0;
            Q0=makeQuery(id+"F9.boolean.opBoolean","MERGE",FACE,{"derivedFrom":[makeQuery(id+"F1.opExtrude","CAP_FACE",FACE,{"disambiguationData":[OSD([sQuery(id+"F0.wireOp",EDGE,"E0.bottom"),sQuery(id+"F0.wireOp",EDGE,"E0.top"),sQuery(id+"F0.wireOp",EDGE,"E0.left"),sQuery(id+"F0.wireOp",EDGE,"E0.right"),sQuery(id+"F0.wireOp",EDGE,"E4"),sQuery(id+"F0.wireOp",EDGE,"E5"),sQuery(id+"F0.wireOp",EDGE,"E6"),sQuery(id+"F0.wireOp",EDGE,"E7"),sQuery(id+"F0.wireOp",EDGE,"E14"),sQuery(id+"F0.wireOp",EDGE,"E15"),sQuery(id+"F0.wireOp",EDGE,"E16"),sQuery(id+"F0.wireOp",EDGE,"E17"),sQuery(id+"F0.wireOp",EDGE,"E23"),sQuery(id+"F0.wireOp",EDGE,"E24"),sQuery(id+"F0.wireOp",EDGE,"E25"),sQuery(id+"F0.wireOp",EDGE,"E26")])],"isStart":false}),makeQuery(id+"F9.opExtrude","CAP_FACE",FACE,{"disambiguationData":[OSD([sQuery(id+"F8.wireOp",EDGE,"E51")])],"isStart":true}),makeQuery(id+"F9.opExtrude","CAP_FACE",FACE,{"disambiguationData":[OSD([sQuery(id+"F8.wireOp",EDGE,"E52")])],"isStart":true})]});
            var sketch = newSketch(context, id + "F10", { "sketchPlane" : qUnion([Q0])});
            skCircle(sketch, "E53", {"center": v(-13.14, 6.5) * mm, "radius": 31 * mm, "construction": true});
            skPoint(sketch, "E53.first.point", {"position": v(-13.14, 37.5) * mm});
            skPoint(sketch, "E53.second.point", {"position": v(17.86, 6.5) * mm});
            skPoint(sketch, "E53.third.point", {"position": v(-35.06, -15.41) * mm});
            skLineSegment(sketch, "E54.0", {"start": v(-13.14, 37.5) * mm, "end": v(13.7, -9) * mm, "construction": true});
            skLineSegment(sketch, "E54.1", {"start": v(13.7, -9) * mm, "end": v(-39.99, -9) * mm, "construction": true});
            skLineSegment(sketch, "E54.2", {"start": v(-39.99, -9) * mm, "end": v(-13.14, 37.5) * mm, "construction": true});
            skCircle(sketch, "E55", {"center": v(-13.14, 37.5) * mm, "radius": 4 * mm});
            skCircle(sketch, "E56", {"center": v(13.7, -9) * mm, "radius": 4 * mm});
            skCircle(sketch, "E57", {"center": v(-39.99, -9) * mm, "radius": 4 * mm});
            skSolve(sketch);
        }
        {
            var Q0;
            Q0=makeQuery(id+"F10.imprint","IMPRINT",FACE,{"disambiguationData":[TD([[makeQuery(id+"F10.imprint","IMPRINT",EDGE,{"derivedFrom":sQuery(id+"F10.wireOp",EDGE,"E56")}),1.0]])]});
            var Q1;
            Q1=makeQuery(id+"F10.imprint","IMPRINT",FACE,{"disambiguationData":[TD([[makeQuery(id+"F10.imprint","IMPRINT",EDGE,{"derivedFrom":sQuery(id+"F10.wireOp",EDGE,"E57")}),1.0]])]});
            var Q2;
            Q2=makeQuery(id+"F10.imprint","IMPRINT",FACE,{"disambiguationData":[TD([[makeQuery(id+"F10.imprint","IMPRINT",EDGE,{"derivedFrom":makeQuery(id+"F5.boolean.opBoolean","COPY",EDGE,{"derivedFrom":makeQuery(id+"F5.opExtrude","CAP_EDGE",EDGE,{"disambiguationData":[OSD([sQuery(id+"F4.wireOp",EDGE,"E40")])],"isStart":true})})}),1.0]])]});
            var Q3;
            Q3=makeQuery(id+"F10.imprint","IMPRINT",FACE,{"disambiguationData":[TD([[makeQuery(id+"F10.imprint","IMPRINT",EDGE,{"derivedFrom":sQuery(id+"F10.wireOp",EDGE,"E55")}),1.0]])]});
            extrude(context, id + "F11", {"entities" : qUnion([Q0, Q1, Q2, Q3]), "operationType" : NewBodyOperationType.REMOVE, "oppositeDirection" : true, "depth" : 1.6 * mm});
        }
        {
            var Q0;
            Q0=makeQuery(id+"F9.boolean.opBoolean","MERGE",FACE,{"derivedFrom":[makeQuery(id+"F1.opExtrude","CAP_FACE",FACE,{"disambiguationData":[OSD([sQuery(id+"F0.wireOp",EDGE,"E0.bottom"),sQuery(id+"F0.wireOp",EDGE,"E0.top"),sQuery(id+"F0.wireOp",EDGE,"E0.left"),sQuery(id+"F0.wireOp",EDGE,"E0.right"),sQuery(id+"F0.wireOp",EDGE,"E4"),sQuery(id+"F0.wireOp",EDGE,"E5"),sQuery(id+"F0.wireOp",EDGE,"E6"),sQuery(id+"F0.wireOp",EDGE,"E7"),sQuery(id+"F0.wireOp",EDGE,"E14"),sQuery(id+"F0.wireOp",EDGE,"E15"),sQuery(id+"F0.wireOp",EDGE,"E16"),sQuery(id+"F0.wireOp",EDGE,"E17"),sQuery(id+"F0.wireOp",EDGE,"E23"),sQuery(id+"F0.wireOp",EDGE,"E24"),sQuery(id+"F0.wireOp",EDGE,"E25"),sQuery(id+"F0.wireOp",EDGE,"E26")])],"isStart":false}),makeQuery(id+"F9.opExtrude","CAP_FACE",FACE,{"disambiguationData":[OSD([sQuery(id+"F8.wireOp",EDGE,"E51")])],"isStart":true}),makeQuery(id+"F9.opExtrude","CAP_FACE",FACE,{"disambiguationData":[OSD([sQuery(id+"F8.wireOp",EDGE,"E52")])],"isStart":true})]});
            var sketch = newSketch(context, id + "F12", { "sketchPlane" : qUnion([Q0])});
            skCircle(sketch, "E58", {"center": v(-35.06, -15.41) * mm, "radius": 3 * mm});
            skCircle(sketch, "E59", {"center": v(8.78, -15.41) * mm, "radius": 3 * mm});
            skSolve(sketch);
        }
        {
            var Q0;
            {var subQ1=makeQuery(id+"F9.opExtrude","CAP_EDGE",EDGE,{"disambiguationData":[OSD([sQuery(id+"F8.wireOp",EDGE,"E52")])],"isStart":true});Q0=makeQuery(id+"F12.imprint","IMPRINT",FACE,{"disambiguationData":[TD([[makeQuery(id+"F12.imprint","IMPRINT",EDGE,{"derivedFrom":subQ1}),1.0]])]});}
            var Q1;
            {var subQ1=makeQuery(id+"F9.opExtrude","CAP_EDGE",EDGE,{"disambiguationData":[OSD([sQuery(id+"F8.wireOp",EDGE,"E52")])],"isStart":true});Q1=makeQuery(id+"F12.imprint","IMPRINT",FACE,{"disambiguationData":[TD([[makeQuery(id+"F12.imprint","IMPRINT",EDGE,{"derivedFrom":subQ1}),-1.0]])]});}
            var Q2;
            {var subQ1=makeQuery(id+"F9.opExtrude","CAP_EDGE",EDGE,{"disambiguationData":[OSD([sQuery(id+"F8.wireOp",EDGE,"E51")])],"isStart":true});Q2=makeQuery(id+"F12.imprint","IMPRINT",FACE,{"disambiguationData":[TD([[makeQuery(id+"F12.imprint","IMPRINT",EDGE,{"derivedFrom":subQ1}),-1.0]])]});}
            var Q3;
            {var subQ1=makeQuery(id+"F9.opExtrude","CAP_EDGE",EDGE,{"disambiguationData":[OSD([sQuery(id+"F8.wireOp",EDGE,"E51")])],"isStart":true});Q3=makeQuery(id+"F12.imprint","IMPRINT",FACE,{"disambiguationData":[TD([[makeQuery(id+"F12.imprint","IMPRINT",EDGE,{"derivedFrom":subQ1}),1.0]])]});}
            extrude(context, id + "F13", {"entities" : qUnion([Q0, Q1, Q2, Q3]), "operationType" : NewBodyOperationType.REMOVE, "oppositeDirection" : true, "depth" : 0.8 * mm});
        }
        {
            var Q0;
            Q0=makeQuery(id+"F9.boolean.opBoolean","MERGE",FACE,{"derivedFrom":[makeQuery(id+"F1.opExtrude","CAP_FACE",FACE,{"disambiguationData":[OSD([sQuery(id+"F0.wireOp",EDGE,"E0.bottom"),sQuery(id+"F0.wireOp",EDGE,"E0.top"),sQuery(id+"F0.wireOp",EDGE,"E0.left"),sQuery(id+"F0.wireOp",EDGE,"E0.right"),sQuery(id+"F0.wireOp",EDGE,"E4"),sQuery(id+"F0.wireOp",EDGE,"E5"),sQuery(id+"F0.wireOp",EDGE,"E6"),sQuery(id+"F0.wireOp",EDGE,"E7"),sQuery(id+"F0.wireOp",EDGE,"E14"),sQuery(id+"F0.wireOp",EDGE,"E15"),sQuery(id+"F0.wireOp",EDGE,"E16"),sQuery(id+"F0.wireOp",EDGE,"E17"),sQuery(id+"F0.wireOp",EDGE,"E23"),sQuery(id+"F0.wireOp",EDGE,"E24"),sQuery(id+"F0.wireOp",EDGE,"E25"),sQuery(id+"F0.wireOp",EDGE,"E26")])],"isStart":false}),makeQuery(id+"F9.opExtrude","CAP_FACE",FACE,{"disambiguationData":[OSD([sQuery(id+"F8.wireOp",EDGE,"E51")])],"isStart":true}),makeQuery(id+"F9.opExtrude","CAP_FACE",FACE,{"disambiguationData":[OSD([sQuery(id+"F8.wireOp",EDGE,"E52")])],"isStart":true})]});
            var sketch = newSketch(context, id + "F14", { "sketchPlane" : qUnion([Q0])});
            skEllipse(sketch, "E60", {"center": v(-44.14, 6.5) * mm, "majorRadius": 4.5 * mm, "minorRadius": 3 * mm, "majorAxis": v(0, 1)});
            skEllipse(sketch, "E61", {"center": v(17.86, 6.5) * mm, "majorRadius": 4.5 * mm, "minorRadius": 3 * mm, "majorAxis": v(0, 1)});
            skSolve(sketch);
        }
        {
            var Q0;
            {var subQ0=sQuery(id+"F14.wireOp",EDGE,"E60");var subQ1=makeQuery(id+"F5.boolean.opBoolean","COPY",EDGE,{"derivedFrom":makeQuery(id+"F5.opExtrude","CAP_EDGE",EDGE,{"disambiguationData":[OSD([sQuery(id+"F4.wireOp",EDGE,"E42")])],"isStart":true})});var subQ2=makeQuery(id+"F14.imprint","INTERSECT",VERTEX,{"disambiguationData":[OD(0.0)],"derivedFrom":[subQ1,subQ0]});Q0=makeQuery(id+"F14.imprint","IMPRINT",FACE,{"disambiguationData":[TD([[makeQuery(id+"F14.imprint","IMPRINT",EDGE,{"disambiguationData":[TD([[subQ2,-1.0]])],"derivedFrom":subQ0}),1.0]])]});}
            var Q1;
            {var subQ0=sQuery(id+"F14.wireOp",EDGE,"E61");var subQ1=makeQuery(id+"F5.boolean.opBoolean","COPY",EDGE,{"derivedFrom":makeQuery(id+"F5.opExtrude","CAP_EDGE",EDGE,{"disambiguationData":[OSD([sQuery(id+"F4.wireOp",EDGE,"E41")])],"isStart":true})});var subQ2=makeQuery(id+"F14.imprint","INTERSECT",VERTEX,{"disambiguationData":[OD(0.0)],"derivedFrom":[subQ1,subQ0]});Q1=makeQuery(id+"F14.imprint","IMPRINT",FACE,{"disambiguationData":[TD([[makeQuery(id+"F14.imprint","IMPRINT",EDGE,{"disambiguationData":[TD([[subQ2,-1.0]])],"derivedFrom":subQ0}),1.0]])]});}
            var Q2;
            {var subQ0=sQuery(id+"F14.wireOp",EDGE,"E61");var subQ1=makeQuery(id+"F5.boolean.opBoolean","COPY",EDGE,{"derivedFrom":makeQuery(id+"F5.opExtrude","CAP_EDGE",EDGE,{"disambiguationData":[OSD([sQuery(id+"F4.wireOp",EDGE,"E41")])],"isStart":true})});var subQ2=makeQuery(id+"F14.imprint","INTERSECT",VERTEX,{"disambiguationData":[OD(0.0)],"derivedFrom":[subQ1,subQ0]});Q2=makeQuery(id+"F14.imprint","IMPRINT",FACE,{"disambiguationData":[TD([[makeQuery(id+"F14.imprint","IMPRINT",EDGE,{"disambiguationData":[TD([[subQ2,1.0]])],"derivedFrom":subQ0}),1.0]])]});}
            var Q3;
            {var subQ0=sQuery(id+"F14.wireOp",EDGE,"E60");var subQ1=makeQuery(id+"F5.boolean.opBoolean","COPY",EDGE,{"derivedFrom":makeQuery(id+"F5.opExtrude","CAP_EDGE",EDGE,{"disambiguationData":[OSD([sQuery(id+"F4.wireOp",EDGE,"E42")])],"isStart":true})});var subQ2=makeQuery(id+"F14.imprint","INTERSECT",VERTEX,{"disambiguationData":[OD(0.0)],"derivedFrom":[subQ1,subQ0]});Q3=makeQuery(id+"F14.imprint","IMPRINT",FACE,{"disambiguationData":[TD([[makeQuery(id+"F14.imprint","IMPRINT",EDGE,{"disambiguationData":[TD([[subQ2,-1.0]])],"derivedFrom":subQ1}),1.0]])]});}
            var Q4;
            {var subQ0=sQuery(id+"F14.wireOp",EDGE,"E61");var subQ1=makeQuery(id+"F5.boolean.opBoolean","COPY",EDGE,{"derivedFrom":makeQuery(id+"F5.opExtrude","CAP_EDGE",EDGE,{"disambiguationData":[OSD([sQuery(id+"F4.wireOp",EDGE,"E41")])],"isStart":true})});var subQ2=makeQuery(id+"F14.imprint","INTERSECT",VERTEX,{"disambiguationData":[OD(0.0)],"derivedFrom":[subQ1,subQ0]});Q4=makeQuery(id+"F14.imprint","IMPRINT",FACE,{"disambiguationData":[TD([[makeQuery(id+"F14.imprint","IMPRINT",EDGE,{"disambiguationData":[TD([[subQ2,-1.0]])],"derivedFrom":subQ1}),1.0]])]});}
            var Q5;
            {var subQ0=sQuery(id+"F14.wireOp",EDGE,"E60");var subQ1=makeQuery(id+"F5.boolean.opBoolean","COPY",EDGE,{"derivedFrom":makeQuery(id+"F5.opExtrude","CAP_EDGE",EDGE,{"disambiguationData":[OSD([sQuery(id+"F4.wireOp",EDGE,"E42")])],"isStart":true})});var subQ2=makeQuery(id+"F14.imprint","INTERSECT",VERTEX,{"disambiguationData":[OD(0.0)],"derivedFrom":[subQ1,subQ0]});Q5=makeQuery(id+"F14.imprint","IMPRINT",FACE,{"disambiguationData":[TD([[makeQuery(id+"F14.imprint","IMPRINT",EDGE,{"disambiguationData":[TD([[subQ2,1.0]])],"derivedFrom":subQ0}),1.0]])]});}
            extrude(context, id + "F15", {"entities" : qUnion([Q0, Q1, Q2, Q3, Q4, Q5]), "operationType" : NewBodyOperationType.REMOVE, "oppositeDirection" : true, "depth" : 25 * mm});
        }
    });
